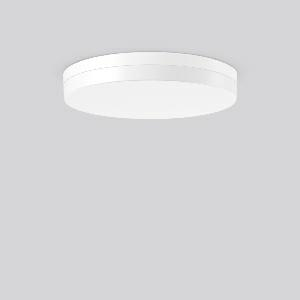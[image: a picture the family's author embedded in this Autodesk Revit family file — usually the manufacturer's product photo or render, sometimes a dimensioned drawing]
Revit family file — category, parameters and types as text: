
# Revit family: flat_slim_round_312678_002_1_19_4a65
name_source: partatom
category: Lighting Fixtures
units: mm (PartAtom-declared; Revit-internal decimal feet)

## family parameters
Cut with Voids When Loaded = No
Host = Face
Light Source = No
Part Type = Normal
Room Calculation Point = No
Round Connector Dimension = Use Diameter
Shared = No

## types (1)
- MultiLumen 1 830 (1 x LED Modul 830, 3500 lm, 3000)
    Apparent Load = 24 VA
    CIE Flux Codes = 38 68 89 85 100
    Color Rendering = 80
    Color Temperature = 3000
    Default Elevation = 1800 mm
    Height = 70 mm
    Lamp = 1 x LED Modul 830
    Lamp Light Flux = 3500 lm
    Lamp count = 1
    Length = 480 mm
    Lifetime = 50000 h
    Luminous efficacy = 146 lm/W
    Manufacturer = RZB
    ModVariant = No
    Model = 312678.002.1.19
    Mounting Place = Ceiling
    Mounting Type = Surface mounted
    Number of Poles = 1
    OnlyDefault = Yes
    Power Factor = 1
    Product Name = FLAT SLIM round
    Product group = Surface mounted ceiling and wall luminaires
    ProductGroupID = 305
    Protection Class = Protection class I
    Protection Degree = Degree of protection
    RLX_Detail_Level = 1
    RLX_Emergency_Light_Flux = 0 lm
    RLX_Emergency_Type = 0
    RLX_Emergency_Type_DB = No
    RlxData = <blob elided: 21809 chars, md5=7b67e598>
    Socket = socket
    Standby Power = 0 W
    System Light Flux = 3500 lm
    System Power = 24 W
    Type Comments = MultiLumen 1 830
    Type Image = 312633.002.jpg
    URL = http://relux.com
    VarID = multilumen_1_830
    Voltage = 0 V
    Weight = 0.00 kg
    Width = 0 mm  [stored 0 ft]

note: [stored X ft] marks values corroborated as IEEE doubles in the binary element streams (Revit-internal decimal feet)

## geometry (parser evidence)
native form markers: Blend x4, Sweep x13
no freeform markers — native parametric forms only
